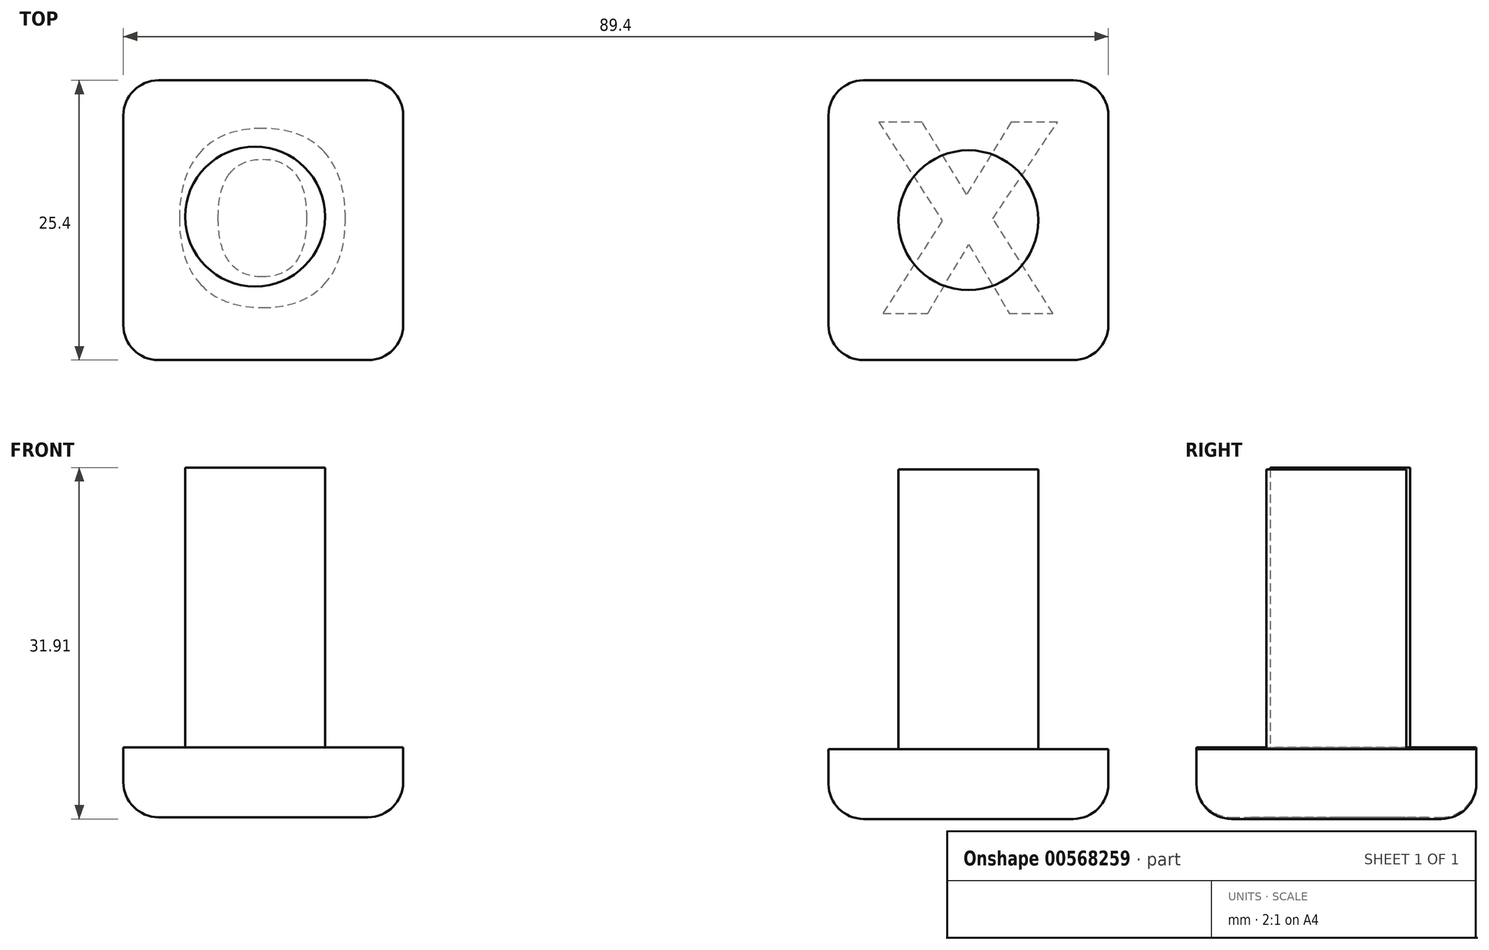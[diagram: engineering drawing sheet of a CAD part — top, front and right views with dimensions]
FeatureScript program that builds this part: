
annotation { "Feature Type Name" : "Feature", "Feature Type Description" : "" }
export const myFeature = defineFeature(function(context is Context, id is Id, definition is map)
    precondition{}
    {
        {
            var Q0;
            Q0=qCreatedBy(makeId("Front.planeOp"),FACE);
            var sketch = newSketch(context, id + "F0", { "sketchPlane" : qUnion([Q0])});
            skLineSegment(sketch, "E0.bottom", {"start": v(17.5, 14.37) * mm, "end": v(42.9, 14.37) * mm});
            skLineSegment(sketch, "E0.top", {"start": v(17.5, 8.02) * mm, "end": v(42.9, 8.02) * mm});
            skLineSegment(sketch, "E0.left", {"start": v(17.5, 14.37) * mm, "end": v(17.5, 8.02) * mm});
            skLineSegment(sketch, "E0.right", {"start": v(42.9, 14.37) * mm, "end": v(42.9, 8.02) * mm});
            skSolve(sketch);
        }
        {
            var Q0;
            Q0=makeQuery(id+"F0.imprint","IMPRINT",FACE,{"disambiguationData":[TD([[makeQuery(id+"F0.imprint","IMPRINT",EDGE,{"derivedFrom":sQuery(id+"F0.wireOp",EDGE,"E0.bottom")}),-1.0]])]});
            extrude(context, id + "F1", {"entities" : qUnion([Q0]), "depth" : 25.4 * mm, "offsetDistance" : 25.4 * mm});
        }
        {
            var Q0;
            Q0=makeQuery(id+"F1.opExtrude","SWEPT_FACE",FACE,{"disambiguationData":[OSD([sQuery(id+"F0.wireOp",EDGE,"E0.bottom")])]});
            var sketch = newSketch(context, id + "F2", { "sketchPlane" : qUnion([Q0])});
            skCircle(sketch, "E1", {"center": v(30.2, -12.7) * mm, "radius": 6.35 * mm});
            skSolve(sketch);
        }
        {
            var Q0;
            Q0=makeQuery(id+"F2.imprint","IMPRINT",FACE,{"disambiguationData":[TD([[makeQuery(id+"F2.imprint","IMPRINT",EDGE,{"derivedFrom":sQuery(id+"F2.wireOp",EDGE,"E1")}),1.0]])]});
            extrude(context, id + "F3", {"entities" : qUnion([Q0]), "operationType" : NewBodyOperationType.ADD, "depth" : 25.4 * mm, "offsetDistance" : 25.4 * mm});
        }
        {
            var Q0;
            Q0=makeQuery(id+"F1.opExtrude","SWEPT_FACE",FACE,{"disambiguationData":[OSD([sQuery(id+"F0.wireOp",EDGE,"E0.top")])]});
            var sketch = newSketch(context, id + "F4", { "sketchPlane" : qUnion([Q0])});
            skText(sketch, "E2", { "text": "X", "fontName": "OpenSans-Bold.ttf"});
            skLineSegment(sketch, "E3", {"start": v(30.2, 25.4) * mm, "end": v(30.96, 0) * mm, "construction": true});
            skLineSegment(sketch, "E4", {"start": v(42.9, 12.55) * mm, "end": v(17.5, 12.55) * mm, "construction": true});
            skPoint(sketch, "E4.startSnap0", {"position": v(39.85, 12.55) * mm});
            const initialGuessF4  = {"E2": [0.02207, 0.0038, 1, 0, 0.0175]};
            skSetInitialGuess(sketch, initialGuessF4);
            skSolve(sketch);
        }
        {
            var Q0;
            Q0 = qSketchRegion(id + "F4", true);
            extrude(context, id + "F5", {"entities" : qUnion([Q0]), "operationType" : NewBodyOperationType.ADD, "depth" : 1 / 203.2 * mm, "offsetDistance" : 25.4 * mm});
        }
        {
            var Q0;
            Q0=qCreatedBy(makeId("Front.planeOp"),FACE);
            var sketch = newSketch(context, id + "F6", { "sketchPlane" : qUnion([Q0])});
            skLineSegment(sketch, "E5.bottom", {"start": v(-46.5, 14.53) * mm, "end": v(-21.1, 14.53) * mm});
            skLineSegment(sketch, "E5.top", {"start": v(-46.5, 8.18) * mm, "end": v(-21.1, 8.18) * mm});
            skLineSegment(sketch, "E5.left", {"start": v(-46.5, 14.53) * mm, "end": v(-46.5, 8.18) * mm});
            skLineSegment(sketch, "E5.right", {"start": v(-21.1, 14.53) * mm, "end": v(-21.1, 8.18) * mm});
            skSolve(sketch);
        }
        {
            var Q0;
            Q0=makeQuery(id+"F6.imprint","IMPRINT",FACE,{"disambiguationData":[TD([[makeQuery(id+"F6.imprint","IMPRINT",EDGE,{"derivedFrom":sQuery(id+"F6.wireOp",EDGE,"E5.bottom")}),-1.0]])]});
            extrude(context, id + "F7", {"entities" : qUnion([Q0]), "depth" : 25.4 * mm, "offsetDistance" : 25.4 * mm});
        }
        {
            var Q0;
            Q0=makeQuery(id+"F7.opExtrude","SWEPT_FACE",FACE,{"disambiguationData":[OSD([sQuery(id+"F6.wireOp",EDGE,"E5.bottom")])]});
            var sketch = newSketch(context, id + "F8", { "sketchPlane" : qUnion([Q0])});
            skCircle(sketch, "E6", {"center": v(-34.55, -12.37) * mm, "radius": 6.35 * mm});
            skSolve(sketch);
        }
        {
            var Q0;
            Q0=makeQuery(id+"F8.imprint","IMPRINT",FACE,{"disambiguationData":[TD([[makeQuery(id+"F8.imprint","IMPRINT",EDGE,{"derivedFrom":sQuery(id+"F8.wireOp",EDGE,"E6")}),1.0]])]});
            extrude(context, id + "F9", {"entities" : qUnion([Q0]), "operationType" : NewBodyOperationType.ADD, "depth" : 25.4 * mm, "offsetDistance" : 25.4 * mm});
        }
        {
            var Q0;
            Q0=makeQuery(id+"F7.opExtrude","SWEPT_FACE",FACE,{"disambiguationData":[OSD([sQuery(id+"F6.wireOp",EDGE,"E5.top")])]});
            var sketch = newSketch(context, id + "F10", { "sketchPlane" : qUnion([Q0])});
            skText(sketch, "E7", { "text": "O", "fontName": "OpenSans-Bold.ttf"});
            const initialGuessF10  = {"E7": [-0.0427, 0.00457, 1, 0, 0.01595]};
            skSetInitialGuess(sketch, initialGuessF10);
            skSolve(sketch);
        }
        {
            var Q0;
            Q0 = qSketchRegion(id + "F10", true);
            extrude(context, id + "F11", {"entities" : qUnion([Q0]), "operationType" : NewBodyOperationType.ADD, "depth" : 1 / 203.2 * mm, "offsetDistance" : 25.4 * mm});
        }
        {
            var Q0;
            Q0=makeQuery(id+"F7.opExtrude","CAP_EDGE",EDGE,{"disambiguationData":[OSD([sQuery(id+"F6.wireOp",EDGE,"E5.top")])],"isStart":false});
            fillet(context, id + "F12", {"entities" : qUnion([Q0]), "radius" : 3.17 * mm, "tangentPropagation" : true, "allowEdgeOverflow" : false});
        }
        {
            var Q0;
            Q0=makeQuery(id+"F7.opExtrude","SWEPT_EDGE",EDGE,{"disambiguationData":[OSD([sQuery(id+"F6.wireOp",EDGE,"E5.top"),sQuery(id+"F6.wireOp",EDGE,"E5.left")])]});
            fillet(context, id + "F13", {"entities" : qUnion([Q0]), "radius" : 3.17 * mm, "tangentPropagation" : true, "allowEdgeOverflow" : false});
        }
        {
            var Q0;
            Q0=makeQuery(id+"F7.opExtrude","CAP_EDGE",EDGE,{"disambiguationData":[OSD([sQuery(id+"F6.wireOp",EDGE,"E5.top")])],"isStart":true});
            fillet(context, id + "F14", {"entities" : qUnion([Q0]), "radius" : 3.17 * mm, "tangentPropagation" : true, "allowEdgeOverflow" : false});
        }
        {
            var Q0;
            Q0=makeQuery(id+"F7.opExtrude","SWEPT_EDGE",EDGE,{"disambiguationData":[OSD([sQuery(id+"F6.wireOp",EDGE,"E5.top"),sQuery(id+"F6.wireOp",EDGE,"E5.right")])]});
            fillet(context, id + "F15", {"entities" : qUnion([Q0]), "radius" : 3.17 * mm, "tangentPropagation" : true, "allowEdgeOverflow" : false});
        }
        {
            var Q0;
            Q0=makeQuery(id+"F1.opExtrude","CAP_EDGE",EDGE,{"disambiguationData":[OSD([sQuery(id+"F0.wireOp",EDGE,"E0.top")])],"isStart":false});
            fillet(context, id + "F16", {"entities" : qUnion([Q0]), "radius" : 3.17 * mm, "tangentPropagation" : true, "allowEdgeOverflow" : false});
        }
        {
            var Q0;
            Q0=makeQuery(id+"F1.opExtrude","SWEPT_EDGE",EDGE,{"disambiguationData":[OSD([sQuery(id+"F0.wireOp",EDGE,"E0.top"),sQuery(id+"F0.wireOp",EDGE,"E0.right")])]});
            fillet(context, id + "F17", {"entities" : qUnion([Q0]), "radius" : 3.17 * mm, "tangentPropagation" : true, "allowEdgeOverflow" : false});
        }
        {
            var Q0;
            Q0=makeQuery(id+"F1.opExtrude","CAP_EDGE",EDGE,{"disambiguationData":[OSD([sQuery(id+"F0.wireOp",EDGE,"E0.top")])],"isStart":true});
            fillet(context, id + "F18", {"entities" : qUnion([Q0]), "radius" : 3.17 * mm, "tangentPropagation" : true, "allowEdgeOverflow" : false});
        }
        {
            var Q0;
            Q0=makeQuery(id+"F1.opExtrude","SWEPT_EDGE",EDGE,{"disambiguationData":[OSD([sQuery(id+"F0.wireOp",EDGE,"E0.top"),sQuery(id+"F0.wireOp",EDGE,"E0.left")])]});
            fillet(context, id + "F19", {"entities" : qUnion([Q0]), "radius" : 3.17 * mm, "tangentPropagation" : true, "allowEdgeOverflow" : false});
        }
    });
